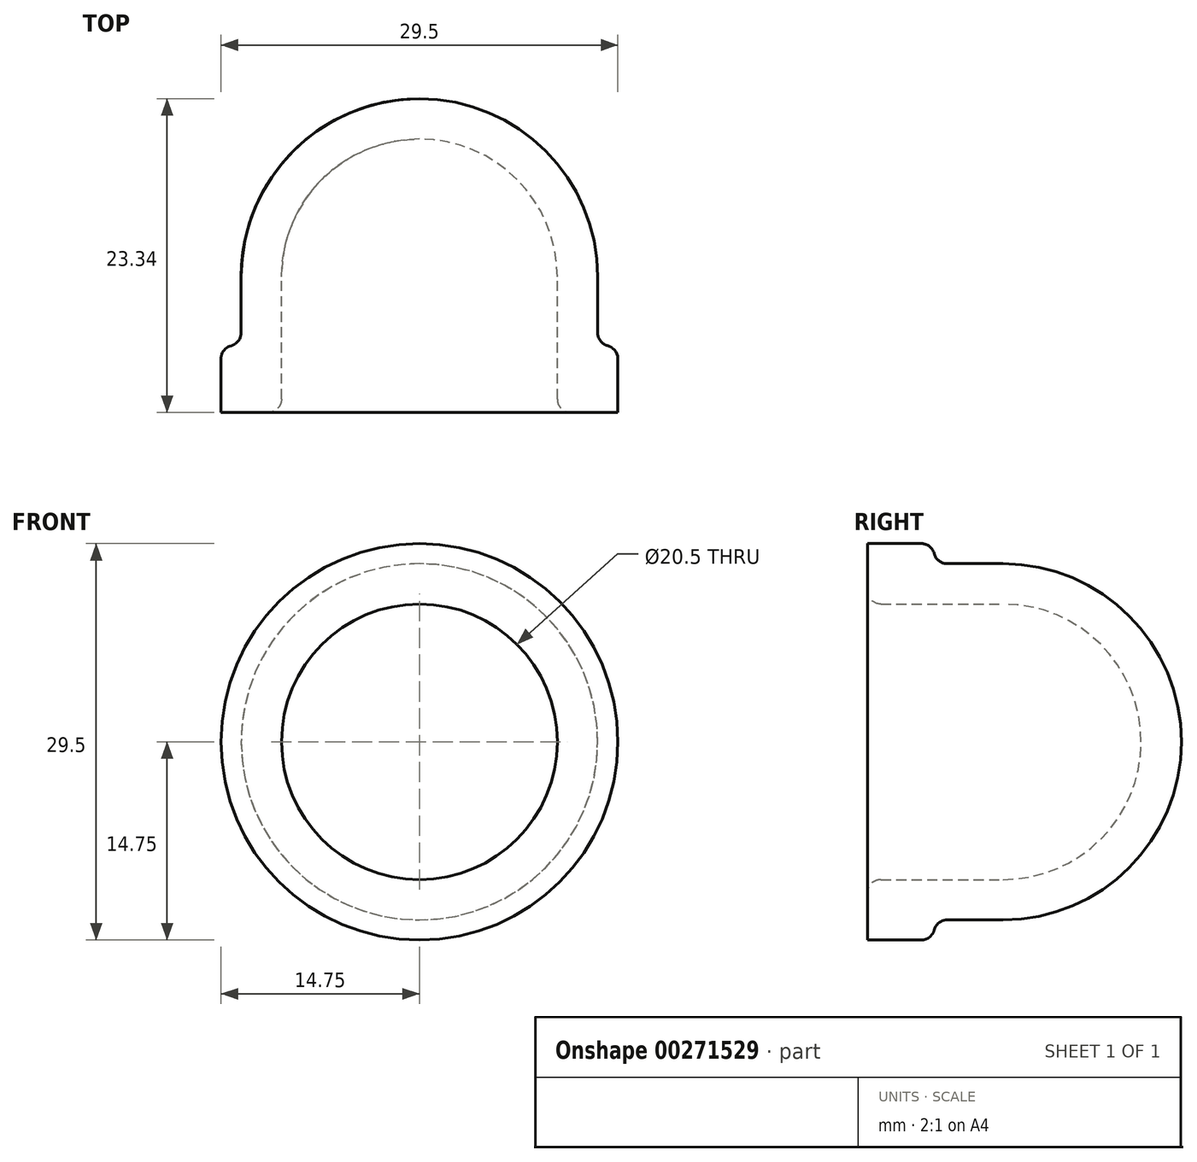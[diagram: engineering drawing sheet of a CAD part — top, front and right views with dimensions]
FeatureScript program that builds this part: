
annotation { "Feature Type Name" : "Feature", "Feature Type Description" : "" }
export const myFeature = defineFeature(function(context is Context, id is Id, definition is map)
    precondition{}
    {
        {
            var Q0;
            Q0=qCreatedBy(makeId("Top.planeOp"),FACE);
            var sketch = newSketch(context, id + "F0", { "sketchPlane" : qUnion([Q0])});
            skArc(sketch, "E0", {"start": v(0, 20.34) * mm, "mid": v(-7.25, 17.34) * mm, "end": v(-10.25, 10.1) * mm});
            skLineSegment(sketch, "E1.top", {"start": v(-10.25, 0) * mm, "end": v(-13.25, 0) * mm});
            skLineSegment(sketch, "E1.left", {"start": v(-10.25, 10.1) * mm, "end": v(-10.25, 0) * mm});
            skLineSegment(sketch, "E1.right", {"start": v(-13.25, 10.87) * mm, "end": v(-13.25, 5) * mm});
            skLineSegment(sketch, "E2.left", {"start": v(0, 23.34) * mm, "end": v(0, 20.34) * mm});
            skArc(sketch, "E3", {"start": v(0, 23.34) * mm, "mid": v(-9.37, 19.46) * mm, "end": v(-13.25, 10.1) * mm});
            skPoint(sketch, "E4.orphan", {"position": v(0, 28.52) * mm});
            skLineSegment(sketch, "E5", {"start": v(0, 33.62) * mm, "end": v(0, -7.76) * mm});
            skLineSegment(sketch, "E6.bottom", {"start": v(-13.25, 0) * mm, "end": v(-14.75, 0) * mm});
            skLineSegment(sketch, "E6.top", {"start": v(-13.25, 5) * mm, "end": v(-14.75, 5) * mm});
            skLineSegment(sketch, "E6.right", {"start": v(-14.75, 0) * mm, "end": v(-14.75, 5) * mm});
            skSolve(sketch);
        }
        {
            var Q0;
            {var subQ3=sQuery(id+"F0.wireOp",EDGE,"E0");Q0=makeQuery(id+"F0.imprint","IMPRINT",FACE,{"disambiguationData":[TD([[makeQuery(id+"F0.imprint","IMPRINT",EDGE,{"derivedFrom":subQ3}),-1.0]])]});}
            var Q1;
            Q1=sQuery(id+"F0.wireOp",EDGE,"E5");
            revolve(context, id + "F1", {"entities" : qUnion([Q0]), "axis" : qUnion([Q1]), "revolveType" : RevolveType.FULL});
        }
        {
            var Q0;
            Q0=makeQuery(id+"F1.opRevolve","SWEPT_EDGE",EDGE,{"disambiguationData":[OSD([sQuery(id+"F0.wireOp",EDGE,"E6.top"),sQuery(id+"F0.wireOp",EDGE,"E6.right")])]});
            fillet(context, id + "F2", {"entities" : qUnion([Q0]), "radius" : 1 * mm, "tangentPropagation" : true, "allowEdgeOverflow" : false});
        }
        {
            var Q0;
            Q0=makeQuery(id+"F1.opRevolve","SWEPT_EDGE",EDGE,{"disambiguationData":[OSD([sQuery(id+"F0.wireOp",EDGE,"E1.top"),sQuery(id+"F0.wireOp",EDGE,"E1.left")])]});
            fillet(context, id + "F3", {"entities" : qUnion([Q0]), "radius" : 1 * mm, "tangentPropagation" : true, "allowEdgeOverflow" : false});
        }
        {
            var Q0;
            Q0=makeQuery(id+"F1.opRevolve","SWEPT_EDGE",EDGE,{"disambiguationData":[OSD([sQuery(id+"F0.wireOp",EDGE,"E1.right"),sQuery(id+"F0.wireOp",EDGE,"E6.top")])]});
            fillet(context, id + "F4", {"entities" : qUnion([Q0]), "radius" : 1 * mm, "tangentPropagation" : true, "allowEdgeOverflow" : false});
        }
    });
